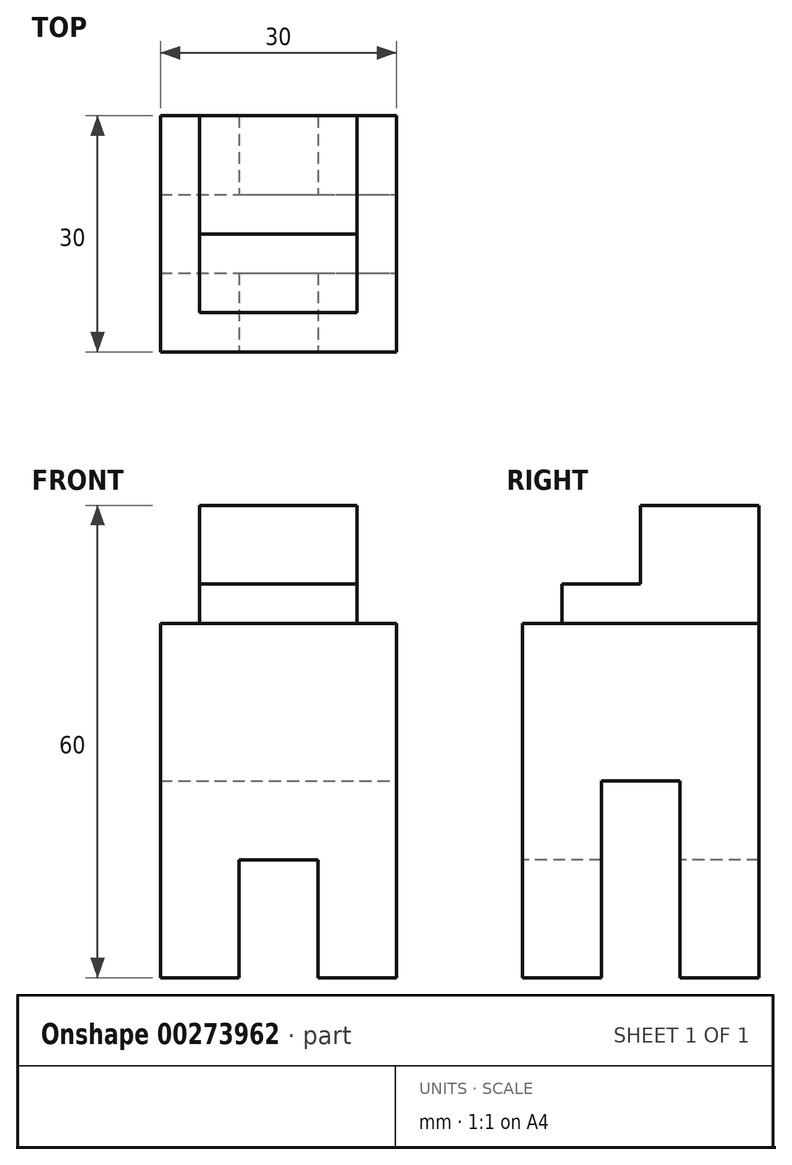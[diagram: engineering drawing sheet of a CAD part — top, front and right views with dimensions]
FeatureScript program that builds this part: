
annotation { "Feature Type Name" : "Feature", "Feature Type Description" : "" }
export const myFeature = defineFeature(function(context is Context, id is Id, definition is map)
    precondition{}
    {
        {
            var Q0;
            Q0=qCreatedBy(makeId("Front.planeOp"),FACE);
            var sketch = newSketch(context, id + "F0", { "sketchPlane" : qUnion([Q0])});
            skLineSegment(sketch, "E0.bottom", {"start": v(-15, 0) * mm, "end": v(15, 0) * mm});
            skLineSegment(sketch, "E0.top", {"start": v(-15, 45) * mm, "end": v(15, 45) * mm});
            skLineSegment(sketch, "E0.left", {"start": v(15, 0) * mm, "end": v(15, 45) * mm});
            skLineSegment(sketch, "E0.right", {"start": v(-15, 0) * mm, "end": v(-15, 45) * mm});
            skSolve(sketch);
        }
        {
            var Q0;
            Q0 = qSketchRegion(id + "F0", true);
            extrude(context, id + "F1", {"entities" : qUnion([Q0]), "endBound" : BoundingType.SYMMETRIC, "depth" : 30 * mm});
        }
        {
            var Q0;
            Q0=makeQuery(id+"F1.opExtrude","CAP_FACE",FACE,{"disambiguationData":[OSD([sQuery(id+"F0.wireOp",EDGE,"E0.bottom"),sQuery(id+"F0.wireOp",EDGE,"E0.top"),sQuery(id+"F0.wireOp",EDGE,"E0.left"),sQuery(id+"F0.wireOp",EDGE,"E0.right")])],"isStart":false});
            var sketch = newSketch(context, id + "F2", { "sketchPlane" : qUnion([Q0])});
            skLineSegment(sketch, "E1.bottom", {"start": v(-5, 0) * mm, "end": v(5, 0) * mm});
            skLineSegment(sketch, "E1.top", {"start": v(-5, 15) * mm, "end": v(5, 15) * mm});
            skLineSegment(sketch, "E1.left", {"start": v(-5, 0) * mm, "end": v(-5, 15) * mm});
            skLineSegment(sketch, "E1.right", {"start": v(5, 0) * mm, "end": v(5, 15) * mm});
            skSolve(sketch);
        }
        {
            var Q0;
            Q0 = qSketchRegion(id + "F2", true);
            extrude(context, id + "F3", {"entities" : qUnion([Q0]), "operationType" : NewBodyOperationType.REMOVE, "endBound" : BoundingType.THROUGH_ALL, "oppositeDirection" : true, "depth" : 25 * mm});
        }
        {
            var Q0;
            Q0=qCreatedBy(makeId("Right.planeOp"),FACE);
            var sketch = newSketch(context, id + "F4", { "sketchPlane" : qUnion([Q0])});
            skLineSegment(sketch, "E2.bottom", {"start": v(-5, 0) * mm, "end": v(5, 0) * mm});
            skLineSegment(sketch, "E2.top", {"start": v(-5, 25) * mm, "end": v(5, 25) * mm});
            skLineSegment(sketch, "E2.left", {"start": v(5, 0) * mm, "end": v(5, 25) * mm});
            skLineSegment(sketch, "E2.right", {"start": v(-5, 0) * mm, "end": v(-5, 25) * mm});
            skSolve(sketch);
        }
        {
            var Q0;
            Q0 = qSketchRegion(id + "F4", true);
            extrude(context, id + "F5", {"entities" : qUnion([Q0]), "operationType" : NewBodyOperationType.REMOVE, "endBound" : BoundingType.THROUGH_ALL, "oppositeDirection" : true, "depth" : 25 * mm, "hasSecondDirection" : true, "secondDirectionBound" : SecondDirectionBoundingType.THROUGH_ALL, "secondDirectionOppositeDirection" : false, "secondDirectionDepth" : 25 * mm});
        }
        {
            var Q0;
            Q0=qCreatedBy(makeId("Right.planeOp"),FACE);
            var sketch = newSketch(context, id + "F6", { "sketchPlane" : qUnion([Q0])});
            skLineSegment(sketch, "E3", {"start": v(15, 60) * mm, "end": v(15, 45) * mm});
            skLineSegment(sketch, "E4", {"start": v(15, 45) * mm, "end": v(-10, 45) * mm});
            skLineSegment(sketch, "E5", {"start": v(-10, 45) * mm, "end": v(-10, 50) * mm});
            skLineSegment(sketch, "E6", {"start": v(-10, 50) * mm, "end": v(0, 50) * mm});
            skLineSegment(sketch, "E7", {"start": v(0, 50) * mm, "end": v(0, 60) * mm});
            skLineSegment(sketch, "E8", {"start": v(0, 60) * mm, "end": v(15, 60) * mm});
            skSolve(sketch);
        }
        {
            var Q0;
            Q0 = qSketchRegion(id + "F6", true);
            extrude(context, id + "F7", {"entities" : qUnion([Q0]), "endBound" : BoundingType.SYMMETRIC, "depth" : 20 * mm});
        }
    });
